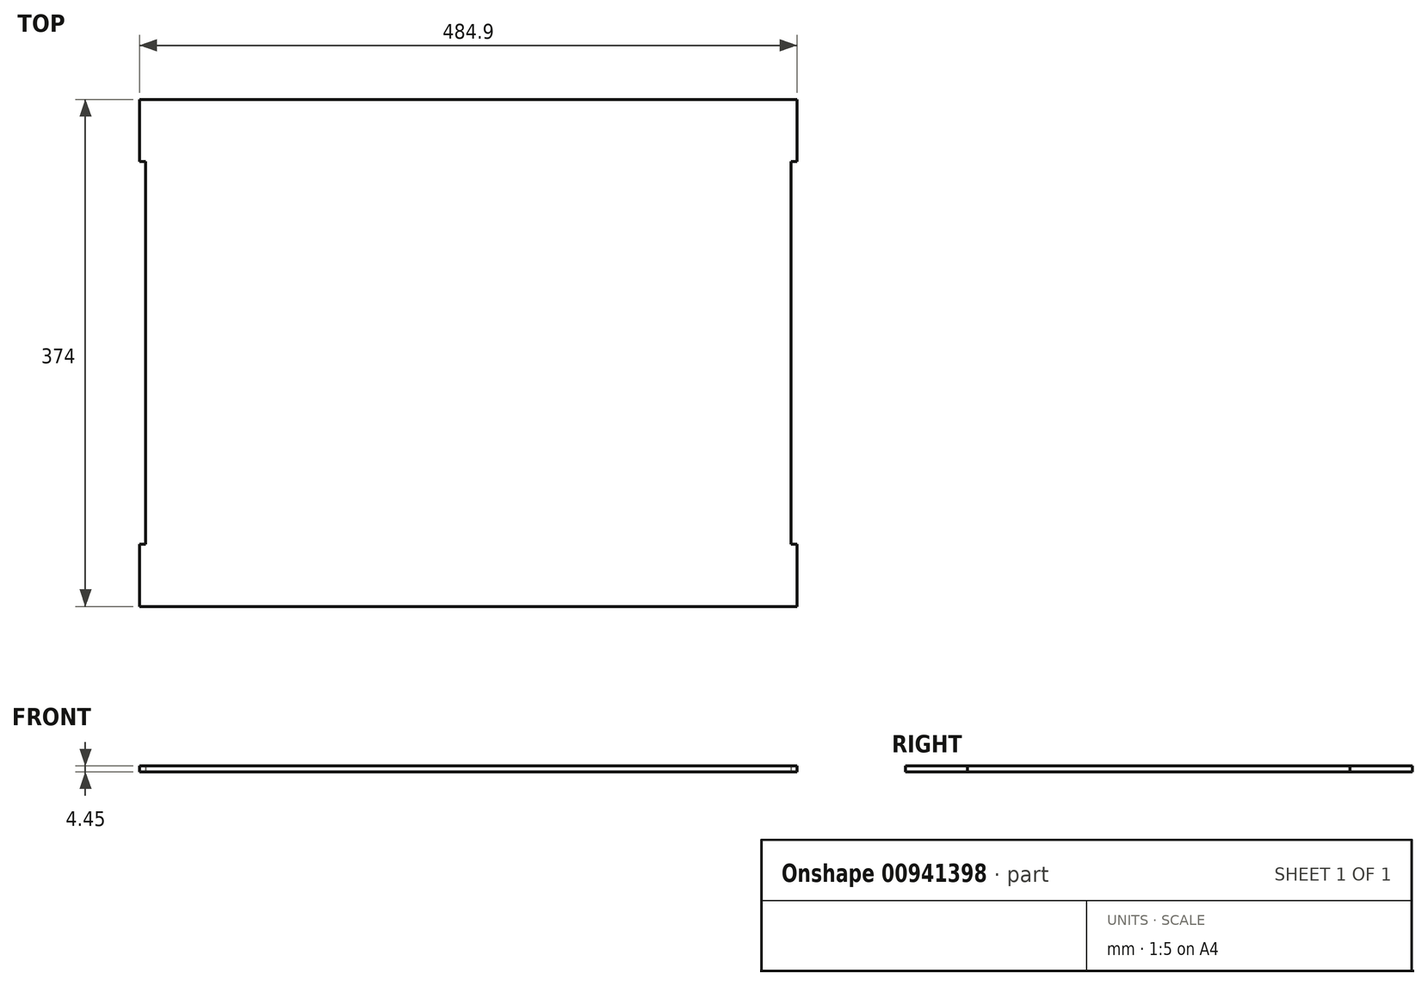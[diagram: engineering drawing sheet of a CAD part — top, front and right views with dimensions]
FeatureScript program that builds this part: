
annotation { "Feature Type Name" : "Feature", "Feature Type Description" : "" }
export const myFeature = defineFeature(function(context is Context, id is Id, definition is map)
    precondition{}
    {
        {
            var Q0;
            Q0=qCreatedBy(makeId("Top.planeOp"),FACE);
            var sketch = newSketch(context, id + "F0", { "sketchPlane" : qUnion([Q0])});
            skLineSegment(sketch, "E0.bottom", {"start": v(238, -187) * mm, "end": v(-238, -187) * mm});
            skLineSegment(sketch, "E0.top", {"start": v(238, 187) * mm, "end": v(-238, 187) * mm});
            skLineSegment(sketch, "E0.left", {"start": v(238, -141.1) * mm, "end": v(238, 141.1) * mm});
            skPoint(sketch, "E0.middle", {"position": v(0, 0) * mm});
            skLineSegment(sketch, "E1.bottom", {"start": v(238, 187) * mm, "end": v(242.45, 187) * mm});
            skLineSegment(sketch, "E1.top", {"start": v(238, 141.1) * mm, "end": v(242.45, 141.1) * mm});
            skLineSegment(sketch, "E1.right", {"start": v(242.45, 187) * mm, "end": v(242.45, 141.1) * mm});
            skLineSegment(sketch, "E2.MirrorCS", {"start": v(238, -141.1) * mm, "end": v(242.45, -141.1) * mm});
            skLineSegment(sketch, "E3.MirrorCS", {"start": v(242.45, -187) * mm, "end": v(242.45, -141.1) * mm});
            skLineSegment(sketch, "E4.MirrorCS", {"start": v(238, -187) * mm, "end": v(242.45, -187) * mm});
            skLineSegment(sketch, "E5.bottom", {"start": v(242.45, -141.1) * mm, "end": v(238, -141.1) * mm});
            skLineSegment(sketch, "E5.top", {"start": v(242.45, 141.1) * mm, "end": v(238, 141.1) * mm});
            skPoint(sketch, "E6.orphan", {"position": v(242.45, -141.1) * mm});
            skPoint(sketch, "E7.orphan", {"position": v(242.45, 141.1) * mm});
            skLineSegment(sketch, "E8.trimOffspring", {"start": v(-238, 141.1) * mm, "end": v(-242.45, 141.1) * mm});
            skLineSegment(sketch, "E9.trimOffspring", {"start": v(-238, -141.1) * mm, "end": v(-242.45, -141.1) * mm});
            skLineSegment(sketch, "E10.MirrorCS", {"start": v(-242.45, 141.1) * mm, "end": v(-238, 141.1) * mm});
            skLineSegment(sketch, "E11.MirrorCS", {"start": v(-242.45, -141.1) * mm, "end": v(-238, -141.1) * mm});
            skLineSegment(sketch, "E12.MirrorCS", {"start": v(-238, 187) * mm, "end": v(238, 187) * mm});
            skLineSegment(sketch, "E13.MirrorCS", {"start": v(-238, -187) * mm, "end": v(238, -187) * mm});
            skLineSegment(sketch, "E14.MirrorCS", {"start": v(-238, -187) * mm, "end": v(-242.45, -187) * mm});
            skLineSegment(sketch, "E15.MirrorCS", {"start": v(-238, 187) * mm, "end": v(-242.45, 187) * mm});
            skPoint(sketch, "E16.MirrorP", {"position": v(-242.45, -141.1) * mm});
            skLineSegment(sketch, "E17.MirrorCS", {"start": v(-242.45, -187) * mm, "end": v(-242.45, -141.1) * mm});
            skPoint(sketch, "E18.MirrorP", {"position": v(-242.45, 141.1) * mm});
            skLineSegment(sketch, "E19.MirrorCS", {"start": v(-242.45, 187) * mm, "end": v(-242.45, 141.1) * mm});
            skLineSegment(sketch, "E20.MirrorCS", {"start": v(-238, -141.1) * mm, "end": v(-238, 141.1) * mm});
            skSolve(sketch);
        }
        {
            var Q0;
            Q0=makeQuery(id+"F0.imprint","IMPRINT",FACE,{"disambiguationData":[TD([[makeQuery(id+"F0.imprint","IMPRINT",EDGE,{"derivedFrom":sQuery(id+"F0.wireOp",EDGE,"E0.bottom")}),-1.0]])]});
            var Q1;
            Q1=makeQuery(id+"F0.imprint","IMPRINT",FACE,{"disambiguationData":[TD([[makeQuery(id+"F0.imprint","IMPRINT",EDGE,{"derivedFrom":sQuery(id+"F0.wireOp",EDGE,"E0.left")}),1.0]])]});
            extrude(context, id + "F1", {"entities" : qUnion([Q0, Q1]), "depth" : 4.45 * mm, "offsetDistance" : 25 * mm});
        }
    });
